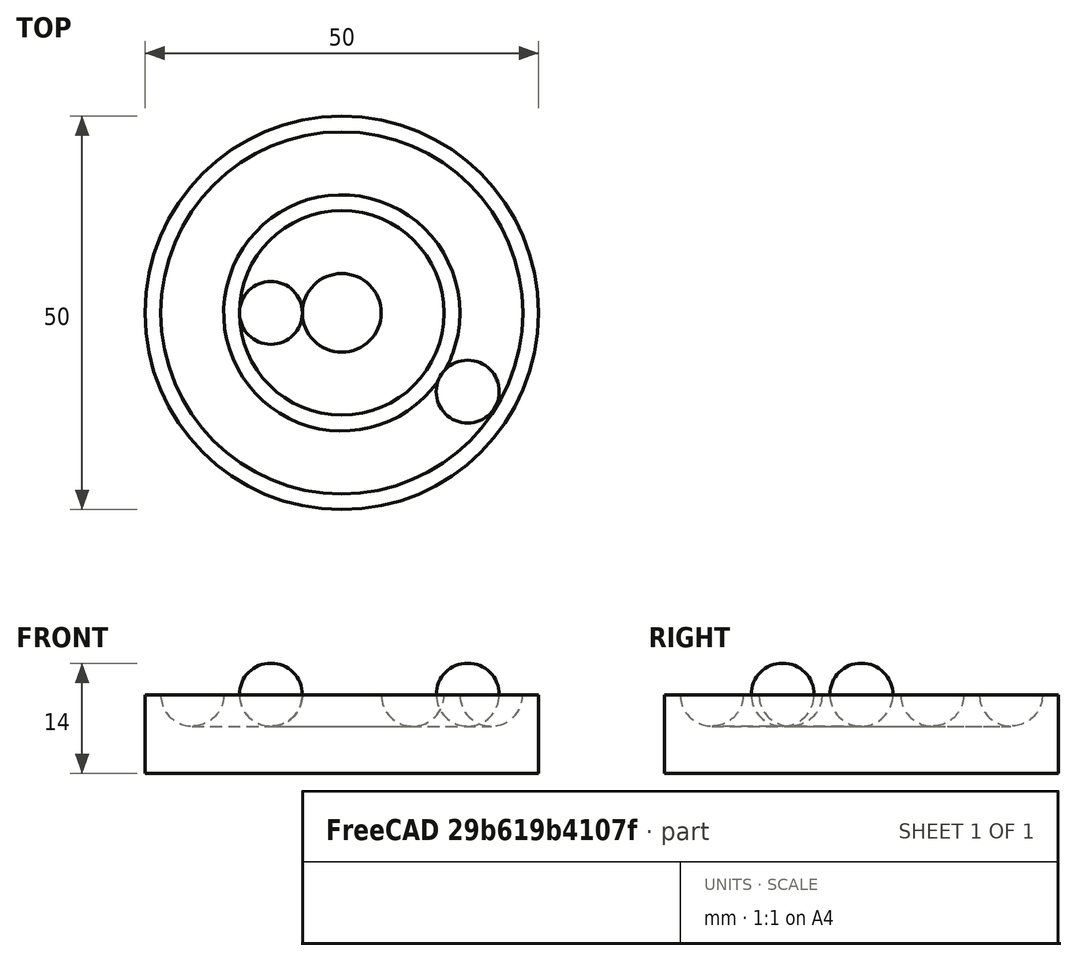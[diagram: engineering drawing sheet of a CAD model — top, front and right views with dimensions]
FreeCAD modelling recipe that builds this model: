
FCSTD DOCUMENT  (FreeCAD 1.0R39319 (Git))
Label: ojt1_t15r02_toolholder
License: All rights reserved
LicenseURL: https://en.wikipedia.org/wiki/All_rights_reserved
objects: Part::Torus×2, Part::Cut×2, Part::Sphere×2, Part::Cylinder×1
note: 7 computed .brp shape members not serialized (recipe doc carries the construction recipe); baked Part::Feature solids carry a one-line shape summary decoded from their .brp

FEATURE [Part::Cylinder] Cylinder  label="Cilindre"
  Angle = 360
  AttacherType = Attacher::AttachEngine3D
  FirstAngle = 0
  Height = 10
  Radius = 25
  SecondAngle = 0
FEATURE [Part::Torus] Torus
  Angle1 = -180
  Angle2 = 180
  Angle3 = 360
  AttacherType = Attacher::AttachEngine3D
  Placement = pos=(0,0,10) rot=(0,0,1;0rad)
  Radius1 = 19
  Radius2 = 4
FEATURE [Part::Torus] Torus001
  Angle1 = -180
  Angle2 = 180
  Angle3 = 360
  AttacherType = Attacher::AttachEngine3D
  Placement = pos=(0,0,10) rot=(0,0,1;0rad)
  Radius1 = 9
  Radius2 = 4
FEATURE [Part::Cut] Cut
  Base = -> Cylinder
  Refine = true
  Tool = -> Torus
FEATURE [Part::Cut] Cut001
  Base = -> Cut
  Refine = true
  Tool = -> Torus001
FEATURE [Part::Sphere] Sphere  label="Esfera"
  Angle1 = -90
  Angle2 = 90
  Angle3 = 360
  AttacherType = Attacher::AttachEngine3D
  Placement = pos=(-9,0,10) rot=(0,0,-1;3.14159rad)
  Radius = 4
FEATURE [Part::Sphere] Sphere001  label="Esfera001"
  Angle1 = -90
  Angle2 = 90
  Angle3 = 360
  AttacherType = Attacher::AttachEngine3D
  Placement = pos=(16,-10,10) rot=(0,0,-1;3.14159rad)
  Radius = 4
